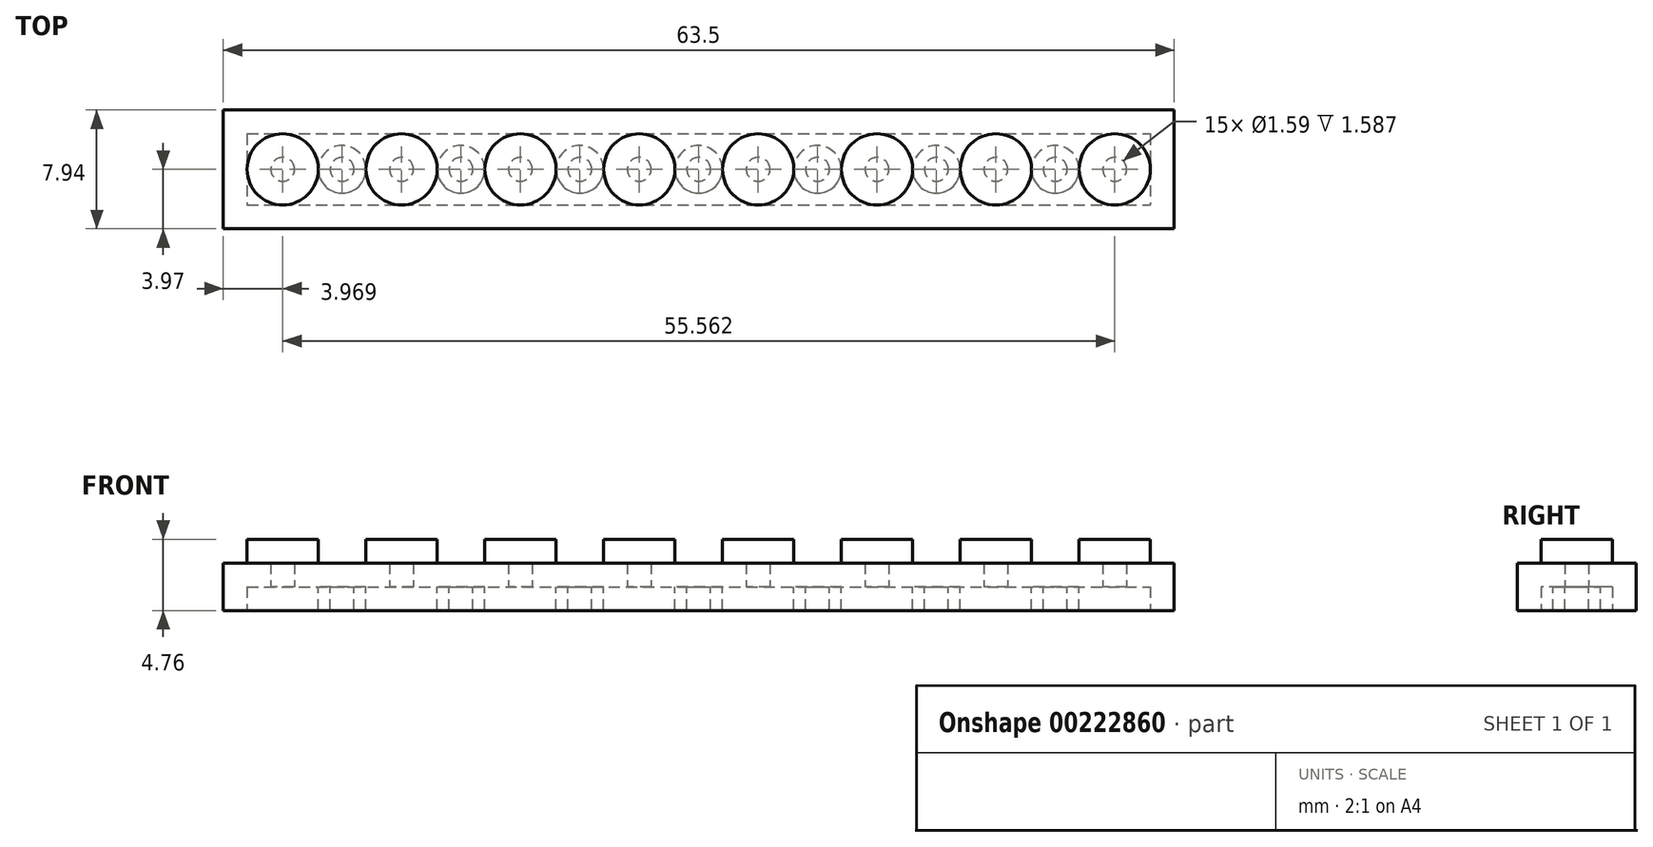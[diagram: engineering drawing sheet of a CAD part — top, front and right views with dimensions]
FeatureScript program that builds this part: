
annotation { "Feature Type Name" : "Feature", "Feature Type Description" : "" }
export const myFeature = defineFeature(function(context is Context, id is Id, definition is map)
    precondition{}
    {
        {
            var Q0;
            Q0=qCreatedBy(makeId("Top.planeOp"),FACE);
            var sketch = newSketch(context, id + "F0", { "sketchPlane" : qUnion([Q0])});
            skLineSegment(sketch, "E0.bottom", {"start": v(-31.75, 3.97) * mm, "end": v(31.75, 3.97) * mm});
            skLineSegment(sketch, "E0.top", {"start": v(-31.75, -3.97) * mm, "end": v(31.75, -3.97) * mm});
            skLineSegment(sketch, "E0.left", {"start": v(-31.75, 3.97) * mm, "end": v(-31.75, -3.97) * mm});
            skLineSegment(sketch, "E0.right", {"start": v(31.75, 3.97) * mm, "end": v(31.75, -3.97) * mm});
            skPoint(sketch, "E0.middle", {"position": v(0, 0) * mm});
            skCircle(sketch, "E1", {"center": v(-27.78, 0) * mm, "radius": 2.38 * mm});
            skCircle(sketch, "E2.1.0.0", {"center": v(-19.84, 0) * mm, "radius": 2.38 * mm});
            skCircle(sketch, "E2.2.0.0", {"center": v(-11.9, 0) * mm, "radius": 2.38 * mm});
            skLineSegment(sketch, "E2.direction1", {"start": v(-27.78, 0) * mm, "end": v(-19.84, 0) * mm, "construction": true});
            skCircle(sketch, "E3.0.3.0", {"center": v(-3.97, 0) * mm, "radius": 2.38 * mm});
            skCircle(sketch, "E4.0.4.0", {"center": v(3.97, 0) * mm, "radius": 2.38 * mm});
            skCircle(sketch, "E4.0.5.0", {"center": v(11.9, 0) * mm, "radius": 2.38 * mm});
            skCircle(sketch, "E4.0.6.0", {"center": v(19.84, 0) * mm, "radius": 2.38 * mm});
            skCircle(sketch, "E4.0.7.0", {"center": v(27.78, 0) * mm, "radius": 2.38 * mm});
            skSolve(sketch);
        }
        {
            var Q0;
            Q0=makeQuery(id+"F0.imprint","IMPRINT",FACE,{"disambiguationData":[TD([[makeQuery(id+"F0.imprint","IMPRINT",EDGE,{"derivedFrom":sQuery(id+"F0.wireOp",EDGE,"E0.bottom")}),-1.0]])]});
            extrude(context, id + "F1", {"entities" : qUnion([Q0]), "depth" : 3.17 * mm});
        }
        {
            var Q0;
            Q0=makeQuery(id+"F0.imprint","IMPRINT",FACE,{"disambiguationData":[TD([[makeQuery(id+"F0.imprint","IMPRINT",EDGE,{"derivedFrom":sQuery(id+"F0.wireOp",EDGE,"8b71ed98-f0e1-4300-85cb-82ad82c44b3e0.MirrorC")}),-1.0]])]});
            var Q1;
            Q1=makeQuery(id+"F0.imprint","IMPRINT",FACE,{"disambiguationData":[TD([[makeQuery(id+"F0.imprint","IMPRINT",EDGE,{"derivedFrom":sQuery(id+"F0.wireOp",EDGE,"E1")}),1.0]])]});
            var Q2;
            Q2=makeQuery(id+"F0.imprint","IMPRINT",FACE,{"disambiguationData":[TD([[makeQuery(id+"F0.imprint","IMPRINT",EDGE,{"derivedFrom":sQuery(id+"F0.wireOp",EDGE,"E2.2.0.0")}),1.0]])]});
            var Q3;
            Q3=makeQuery(id+"F0.imprint","IMPRINT",FACE,{"disambiguationData":[TD([[makeQuery(id+"F0.imprint","IMPRINT",EDGE,{"derivedFrom":sQuery(id+"F0.wireOp",EDGE,"E2.1.0.0")}),1.0]])]});
            var Q4;
            Q4=makeQuery(id+"F0.imprint","IMPRINT",FACE,{"disambiguationData":[TD([[makeQuery(id+"F0.imprint","IMPRINT",EDGE,{"derivedFrom":sQuery(id+"F0.wireOp",EDGE,"E3.0.3.0")}),1.0]])]});
            var Q5;
            Q5=makeQuery(id+"F0.imprint","IMPRINT",FACE,{"disambiguationData":[TD([[makeQuery(id+"F0.imprint","IMPRINT",EDGE,{"derivedFrom":sQuery(id+"F0.wireOp",EDGE,"E4.0.4.0")}),1.0]])]});
            var Q6;
            Q6=makeQuery(id+"F0.imprint","IMPRINT",FACE,{"disambiguationData":[TD([[makeQuery(id+"F0.imprint","IMPRINT",EDGE,{"derivedFrom":sQuery(id+"F0.wireOp",EDGE,"E4.0.5.0")}),1.0]])]});
            var Q7;
            Q7=makeQuery(id+"F0.imprint","IMPRINT",FACE,{"disambiguationData":[TD([[makeQuery(id+"F0.imprint","IMPRINT",EDGE,{"derivedFrom":sQuery(id+"F0.wireOp",EDGE,"E4.0.6.0")}),1.0]])]});
            var Q8;
            Q8=makeQuery(id+"F0.imprint","IMPRINT",FACE,{"disambiguationData":[TD([[makeQuery(id+"F0.imprint","IMPRINT",EDGE,{"derivedFrom":sQuery(id+"F0.wireOp",EDGE,"E4.0.7.0")}),1.0]])]});
            extrude(context, id + "F2", {"entities" : qUnion([Q0, Q1, Q2, Q3, Q4, Q5, Q6, Q7, Q8]), "operationType" : NewBodyOperationType.ADD, "depth" : 4.76 * mm});
        }
        {
            var Q0;
            {var subQ0=sQuery(id+"F0.wireOp",EDGE,"8b71ed98-f0e1-4300-85cb-82ad82c44b3e0.MirrorC");var subQ1=sQuery(id+"F0.wireOp",EDGE,"E1");Q0=makeQuery(id+"F2.boolean.opBoolean","MERGE",FACE,{"derivedFrom":[makeQuery(id+"F1.opExtrude","CAP_FACE",FACE,{"disambiguationData":[OSD([sQuery(id+"F0.wireOp",EDGE,"E0.bottom"),sQuery(id+"F0.wireOp",EDGE,"E0.top"),sQuery(id+"F0.wireOp",EDGE,"E0.left"),sQuery(id+"F0.wireOp",EDGE,"E0.right"),subQ1,subQ0])],"isStart":true}),makeQuery(id+"F2.opExtrude","CAP_FACE",FACE,{"disambiguationData":[OSD([subQ1])],"isStart":true}),makeQuery(id+"F2.opExtrude","CAP_FACE",FACE,{"disambiguationData":[OSD([subQ0])],"isStart":true})]});}
            shell(context, id + "F3", {"entities" : qUnion([Q0]), "thickness" : 1.59 * mm});
        }
        {
            var Q0;
            Q0=makeQuery(id+"F3.opShell","OFFSET_FACE",FACE,{"disambiguationData":[OSD([sQuery(id+"F0.wireOp",EDGE,"E0.bottom"),sQuery(id+"F0.wireOp",EDGE,"E0.top"),sQuery(id+"F0.wireOp",EDGE,"E0.left"),sQuery(id+"F0.wireOp",EDGE,"E0.right"),sQuery(id+"F0.wireOp",EDGE,"E1"),sQuery(id+"F0.wireOp",EDGE,"8b71ed98-f0e1-4300-85cb-82ad82c44b3e0.MirrorC")])]});
            var sketch = newSketch(context, id + "F4", { "sketchPlane" : qUnion([Q0])});
            skCircle(sketch, "E5.1.0.0", {"center": v(-23.81, 0) * mm, "radius": 1.59 * mm});
            skCircle(sketch, "E5.1.0.1", {"center": v(-23.81, 0) * mm, "radius": 0.8 * mm});
            skCircle(sketch, "E6.1.0.0", {"center": v(-15.88, 0) * mm, "radius": 1.59 * mm});
            skCircle(sketch, "E6.1.0.1", {"center": v(-15.88, 0) * mm, "radius": 0.8 * mm});
            skCircle(sketch, "E6.2.0.0", {"center": v(-7.94, 0) * mm, "radius": 1.59 * mm});
            skCircle(sketch, "E6.2.0.1", {"center": v(-7.94, 0) * mm, "radius": 0.8 * mm});
            skCircle(sketch, "E6.3.0.0", {"center": v(0, 0) * mm, "radius": 1.59 * mm});
            skCircle(sketch, "E6.3.0.1", {"center": v(0, 0) * mm, "radius": 0.8 * mm});
            skCircle(sketch, "E6.4.0.0", {"center": v(7.94, 0) * mm, "radius": 1.59 * mm});
            skCircle(sketch, "E6.4.0.1", {"center": v(7.94, 0) * mm, "radius": 0.8 * mm});
            skCircle(sketch, "E6.5.0.0", {"center": v(15.87, 0) * mm, "radius": 1.59 * mm});
            skCircle(sketch, "E6.5.0.1", {"center": v(15.87, 0) * mm, "radius": 0.8 * mm});
            skCircle(sketch, "E6.6.0.0", {"center": v(23.81, 0) * mm, "radius": 1.59 * mm});
            skCircle(sketch, "E6.6.0.1", {"center": v(23.81, 0) * mm, "radius": 0.8 * mm});
            skLineSegment(sketch, "E6.direction1", {"start": v(-23.81, 0) * mm, "end": v(-15.88, 0) * mm, "construction": true});
            skSolve(sketch);
        }
        {
            var Q0;
            Q0=makeQuery(id+"F4.imprint","IMPRINT",FACE,{"disambiguationData":[TD([[makeQuery(id+"F4.imprint","IMPRINT",EDGE,{"derivedFrom":sQuery(id+"F4.wireOp",EDGE,"E5.1.0.0")}),1.0]])]});
            var Q1;
            Q1=makeQuery(id+"F4.imprint","IMPRINT",FACE,{"disambiguationData":[TD([[makeQuery(id+"F4.imprint","IMPRINT",EDGE,{"derivedFrom":sQuery(id+"F4.wireOp",EDGE,"E6.1.0.0")}),1.0]])]});
            var Q2;
            Q2=makeQuery(id+"F4.imprint","IMPRINT",FACE,{"disambiguationData":[TD([[makeQuery(id+"F4.imprint","IMPRINT",EDGE,{"derivedFrom":sQuery(id+"F4.wireOp",EDGE,"E6.2.0.0")}),1.0]])]});
            var Q3;
            Q3=makeQuery(id+"F4.imprint","IMPRINT",FACE,{"disambiguationData":[TD([[makeQuery(id+"F4.imprint","IMPRINT",EDGE,{"derivedFrom":sQuery(id+"F4.wireOp",EDGE,"E6.3.0.0")}),1.0]])]});
            var Q4;
            Q4=makeQuery(id+"F4.imprint","IMPRINT",FACE,{"disambiguationData":[TD([[makeQuery(id+"F4.imprint","IMPRINT",EDGE,{"derivedFrom":sQuery(id+"F4.wireOp",EDGE,"E6.4.0.0")}),1.0]])]});
            var Q5;
            Q5=makeQuery(id+"F4.imprint","IMPRINT",FACE,{"disambiguationData":[TD([[makeQuery(id+"F4.imprint","IMPRINT",EDGE,{"derivedFrom":sQuery(id+"F4.wireOp",EDGE,"E6.5.0.0")}),1.0]])]});
            var Q6;
            Q6=makeQuery(id+"F4.imprint","IMPRINT",FACE,{"disambiguationData":[TD([[makeQuery(id+"F4.imprint","IMPRINT",EDGE,{"derivedFrom":sQuery(id+"F4.wireOp",EDGE,"E6.6.0.0")}),1.0]])]});
            extrude(context, id + "F5", {"entities" : qUnion([Q0, Q1, Q2, Q3, Q4, Q5, Q6]), "operationType" : NewBodyOperationType.ADD, "depth" : 1.59 * mm});
        }
    });
